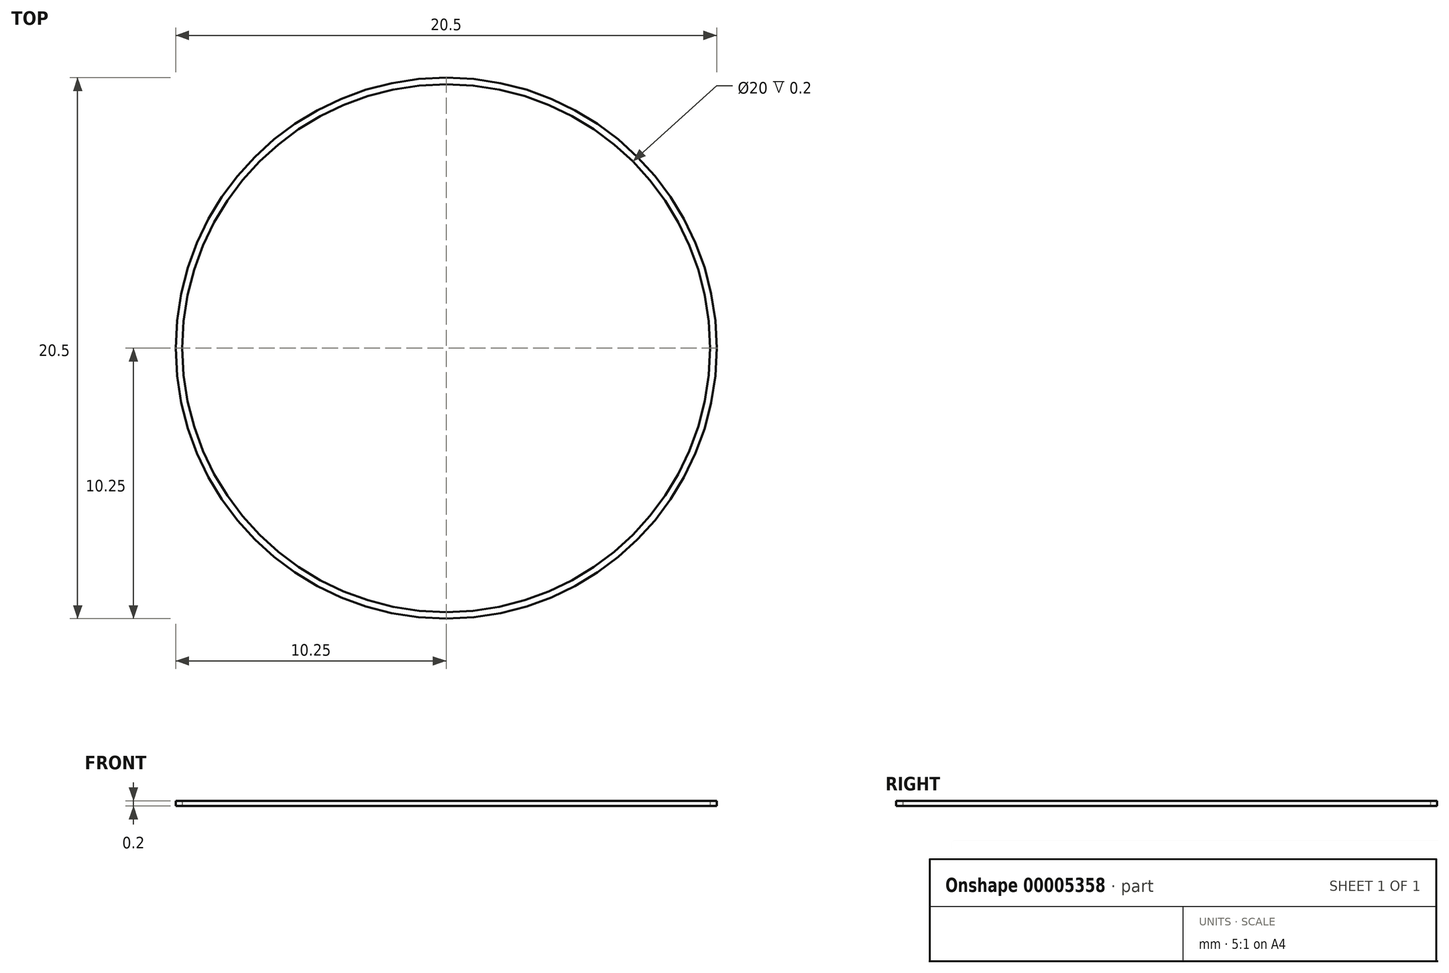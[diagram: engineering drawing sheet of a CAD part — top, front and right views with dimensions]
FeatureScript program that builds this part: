
annotation { "Feature Type Name" : "Feature", "Feature Type Description" : "" }
export const myFeature = defineFeature(function(context is Context, id is Id, definition is map)
    precondition{}
    {
        {
            var Q0;
            Q0=qCreatedBy(makeId("Top.planeOp"),FACE);
            var sketch = newSketch(context, id + "F0", { "sketchPlane" : qUnion([Q0])});
            skCircle(sketch, "E0", {"center": v(0, 0) * mm, "radius": 10 * mm});
            skCircle(sketch, "E1", {"center": v(0, 0) * mm, "radius": 10.25 * mm});
            skSolve(sketch);
        }
        {
            var Q0;
            Q0=makeQuery(id+"F0.imprint","IMPRINT",FACE,{"disambiguationData":[TD([[makeQuery(id+"F0.imprint","IMPRINT",EDGE,{"derivedFrom":sQuery(id+"F0.wireOp",EDGE,"E0")}),-1.0]])]});
            extrude(context, id + "F1", {"entities" : qUnion([Q0]), "depth" : .2 * mm});
        }
    });
